# Revit family: Spout-American_Standard-Delancey-8888_Series
name_source: partatom
category: Plumbing Fixtures
revit_build: Autodesk Revit 2014 (Build: 20130308_1515(x64)
units: mm (PartAtom-declared; Revit-internal decimal feet)

## types (16) — shared parameters
Assembly Code = D2020300
CW Connection = Yes
CWFU = 3
Connection Description = 1/2" Slip-On Supply Inlet
Default Elevation = 21"
Description = Delancey Tub Spout
HW Connection = Yes
HWFU = 3
Height = 3 1/2"
Installation Type = Wall Mounted
Length = 8"
Manufacturer = American Standard
Price = Prices may vary. Please consult Manufacturer Representative for most up-to-date price list.
URL = https://www.americanstandard-us.com
Vent Connection = No
WFU = 4
Warranty Information = Limited Lifetime Function and Finish Warranty
Waste Connection = No
Water Connection Diameter = 1/2"
Water Connection Radius = 1/4"
Width = 3 1/2"

## per-type parameters (varying)
| type | Diverter | Finish | Material |
| 8888107.002 | No | Metal-American Standard-002-Polished Chrome | Metal-American Standard-002-Polished Chrome |
| 8888107.013 | No | Metal-American Standard-013-Polished Nickel | Metal-American Standard-013-Polished Nickel |
| 8888107.295 | No | Metal-American Standard-295-Brushed Nickel | Metal-American Standard-295-Brushed Nickel |
| 8888107.278 | No | Metal-American Standard-278-Legacy Bronze | Metal-American Standard-278-Legacy Bronze |
| 8888106.002 | No | Metal-American Standard-002-Polished Chrome | Metal-American Standard-002-Polished Chrome |
| 8888106.013 | No | Metal-American Standard-013-Polished Nickel | Metal-American Standard-013-Polished Nickel |
| 8888106.278 | No | Metal-American Standard-278-Legacy Bronze | Metal-American Standard-278-Legacy Bronze |
| 8888106.295 | No | Metal-American Standard-295-Brushed Nickel | Metal-American Standard-295-Brushed Nickel |
| 8888105.002 | Yes | Metal-American Standard-002-Polished Chrome | Metal-American Standard-002-Polished Chrome |
| 8888105.013 | Yes | Metal-American Standard-013-Polished Nickel | Metal-American Standard-013-Polished Nickel |
| 8888105.278 | Yes | Metal-American Standard-278-Legacy Bronze | Metal-American Standard-278-Legacy Bronze |
| 8888105.295 | Yes | Metal-American Standard-295-Brushed Nickel | Metal-American Standard-295-Brushed Nickel |
| 8888104.002 | Yes | Metal-American Standard-002-Polished Chrome | Metal-American Standard-002-Polished Chrome |
| 8888104.013 | Yes | Metal-American Standard-013-Polished Nickel | Metal-American Standard-013-Polished Nickel |
| 8888104.278 | Yes | Metal-American Standard-278-Legacy Bronze | Metal-American Standard-278-Legacy Bronze |
| 8888104.295 | Yes | Metal-American Standard-295-Brushed Nickel | Metal-American Standard-295-Brushed Nickel |

note: column(s) folded — value = type name in every type: Model

## geometry (parser evidence)
native form markers: Sweep x3
no freeform markers — native parametric forms only
